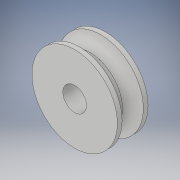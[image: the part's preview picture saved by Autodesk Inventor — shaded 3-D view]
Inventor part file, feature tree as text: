
AUTODESK INVENTOR PART (.ipt)
format: ipt  version: 2019 (Build 230136000, 136)  size: 154,112 bytes
history: native  units: in
note: dims shown in document units (in); Inventor stores cm internally (conversion verified against a paired STEP export)
features: sketch x3, extrude x2, hole x1, mirror x1, fillet x1
ambient origin geometry x8: Origin, YZ Plane, XZ Plane, XY Plane, X Axis, Y Axis, Z Axis, Center Point
bodies: Solid1 (feature_tree)
feature tree (8):
  extrude  "Extrusion1"  Depth=0.04in TaperAngle=0.0deg
  extrude  "Extrusion2"  Depth=0.09in TaperAngle=0.0deg
  hole  "Hole1"  [1 undecoded]
  mirror  "Mirror1"
  fillet  "Fillet1"  [1 undecoded]
  sketch  "Sketch1"  dims[d0=0.723in d1=0.04in d2=0.0in]
  sketch  "Sketch2"  dims[d3=0.55in d4=0.09in d5=0.0in]
  sketch  "Sketch3"  dims[d6=0.2in d7=0.75in d8=0.375in d9=0.25in d10=0.5635in d11=1.0in d12=0.8108in d13=0.09in]
note: 2 required parameter values undecoded (feature->parameter linkage not recoverable at this tier; creation-order binding heuristic only, values carry confidence <= 0.55)
